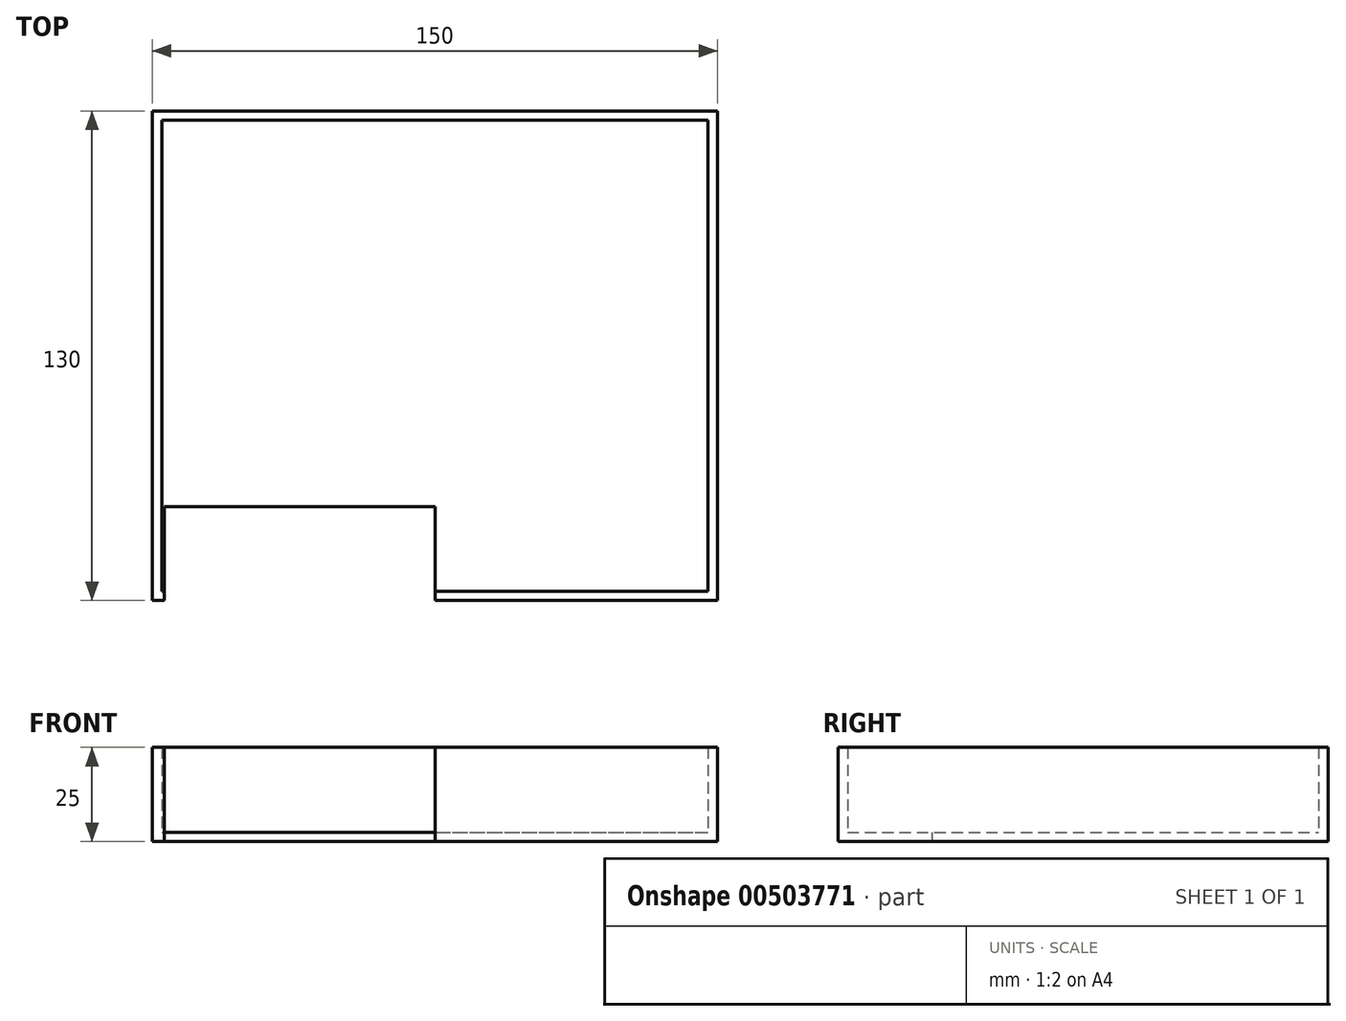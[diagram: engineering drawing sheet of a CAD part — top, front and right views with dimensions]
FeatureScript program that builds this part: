
annotation { "Feature Type Name" : "Feature", "Feature Type Description" : "" }
export const myFeature = defineFeature(function(context is Context, id is Id, definition is map)
    precondition{}
    {
        {
            var Q0;
            Q0=qCreatedBy(makeId("Top.planeOp"),FACE);
            var sketch = newSketch(context, id + "F0", { "sketchPlane" : qUnion([Q0])});
            skLineSegment(sketch, "E0.bottom", {"start": v(-75, -65) * mm, "end": v(75, -65) * mm});
            skLineSegment(sketch, "E0.top", {"start": v(-75, 65) * mm, "end": v(75, 65) * mm});
            skLineSegment(sketch, "E0.left", {"start": v(-75, -65) * mm, "end": v(-75, 65) * mm});
            skLineSegment(sketch, "E0.right", {"start": v(75, -65) * mm, "end": v(75, 65) * mm});
            skPoint(sketch, "E0.middle", {"position": v(0, 0) * mm});
            skSolve(sketch);
        }
        {
            var Q0;
            Q0=makeQuery(id+"F0.imprint","IMPRINT",FACE,{"disambiguationData":[TD([[makeQuery(id+"F0.imprint","IMPRINT",EDGE,{"derivedFrom":sQuery(id+"F0.wireOp",EDGE,"E0.bottom")}),1.0]])]});
            extrude(context, id + "F1", {"entities" : qUnion([Q0]), "depth" : 25 * mm});
        }
        {
            var Q0;
            Q0=makeQuery(id+"F1.opExtrude","CAP_FACE",FACE,{"disambiguationData":[OSD([sQuery(id+"F0.wireOp",EDGE,"E0.bottom"),sQuery(id+"F0.wireOp",EDGE,"E0.top"),sQuery(id+"F0.wireOp",EDGE,"E0.left"),sQuery(id+"F0.wireOp",EDGE,"E0.right")])],"isStart":false});
            shell(context, id + "F2", {"entities" : qUnion([Q0]), "thickness" : 2.5 * mm});
        }
        {
            var Q0;
            Q0=makeQuery(id+"F1.opExtrude","SWEPT_FACE",FACE,{"disambiguationData":[OSD([sQuery(id+"F0.wireOp",EDGE,"E0.bottom")])]});
            var sketch = newSketch(context, id + "F3", { "sketchPlane" : qUnion([Q0])});
            skLineSegment(sketch, "E1.bottom", {"start": v(0, 0) * mm, "end": v(-71.86, 0) * mm});
            skLineSegment(sketch, "E1.top", {"start": v(0, 25) * mm, "end": v(-71.86, 25) * mm});
            skLineSegment(sketch, "E1.left", {"start": v(0, 0) * mm, "end": v(0, 25) * mm});
            skLineSegment(sketch, "E1.right", {"start": v(-71.86, 0) * mm, "end": v(-71.86, 25) * mm});
            skSolve(sketch);
        }
        {
            var Q0;
            Q0=makeQuery(id+"F3.imprint","IMPRINT",FACE,{"disambiguationData":[TD([[makeQuery(id+"F3.imprint","IMPRINT",EDGE,{"derivedFrom":sQuery(id+"F3.wireOp",EDGE,"E1.bottom")}),1.0]])]});
            extrude(context, id + "F4", {"entities" : qUnion([Q0]), "operationType" : NewBodyOperationType.REMOVE, "oppositeDirection" : true, "depth" : 25 * mm});
        }
    });
